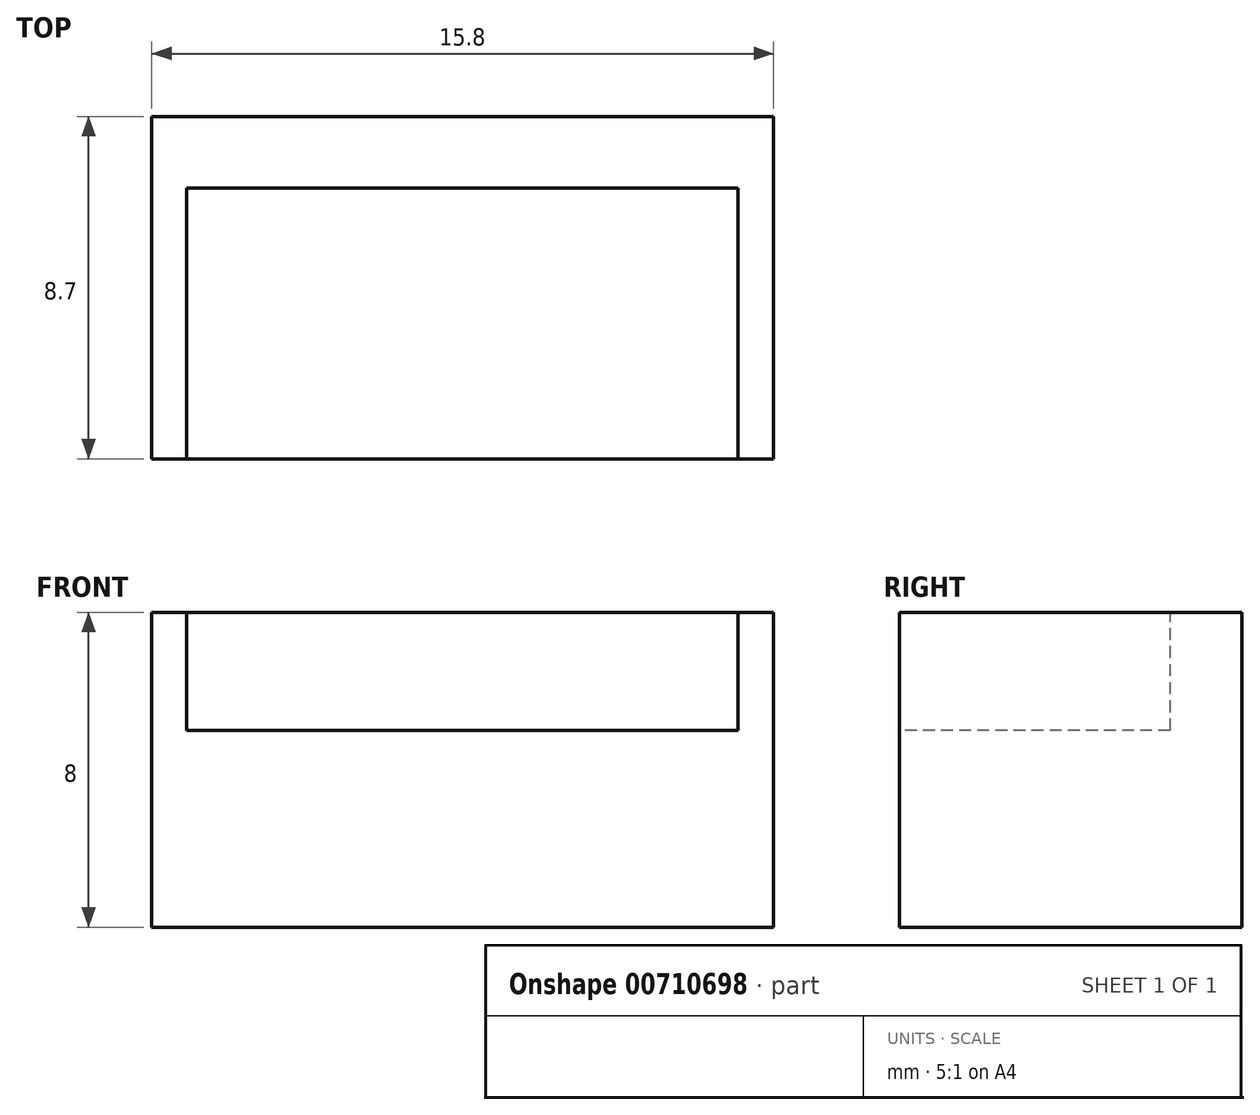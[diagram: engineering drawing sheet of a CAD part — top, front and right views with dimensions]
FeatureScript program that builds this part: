
annotation { "Feature Type Name" : "Feature", "Feature Type Description" : "" }
export const myFeature = defineFeature(function(context is Context, id is Id, definition is map)
    precondition{}
    {
        {
            var Q0;
            Q0=qCreatedBy(makeId("Top.planeOp"),FACE);
            var sketch = newSketch(context, id + "F0", { "sketchPlane" : qUnion([Q0])});
            skLineSegment(sketch, "E0.bottom", {"start": v(0, 0) * mm, "end": v(15.8, 0) * mm});
            skLineSegment(sketch, "E0.top", {"start": v(0, -8.7) * mm, "end": v(15.8, -8.7) * mm});
            skLineSegment(sketch, "E0.left", {"start": v(0, 0) * mm, "end": v(0, -8.7) * mm});
            skLineSegment(sketch, "E0.right", {"start": v(15.8, 0) * mm, "end": v(15.8, -8.7) * mm});
            skSolve(sketch);
        }
        {
            var Q0;
            Q0=makeQuery(id+"F0.imprint","IMPRINT",FACE,{"disambiguationData":[TD([[makeQuery(id+"F0.imprint","IMPRINT",EDGE,{"derivedFrom":sQuery(id+"F0.wireOp",EDGE,"E0.bottom")}),-1.0]])]});
            extrude(context, id + "F1", {"entities" : qUnion([Q0]), "depth" : 8 * mm, "offsetDistance" : 25 * mm});
        }
        {
            var Q0;
            Q0=makeQuery(id+"F1.opExtrude","CAP_FACE",FACE,{"disambiguationData":[OSD([sQuery(id+"F0.wireOp",EDGE,"E0.bottom"),sQuery(id+"F0.wireOp",EDGE,"E0.top"),sQuery(id+"F0.wireOp",EDGE,"E0.left"),sQuery(id+"F0.wireOp",EDGE,"E0.right")])],"isStart":false});
            var sketch = newSketch(context, id + "F2", { "sketchPlane" : qUnion([Q0])});
            skLineSegment(sketch, "E1.0", {"start": v(0, -8.7) * mm, "end": v(15.8, -8.7) * mm});
            skLineSegment(sketch, "E2.bottom", {"start": v(0.9, -1.82) * mm, "end": v(14.9, -1.82) * mm});
            skLineSegment(sketch, "E2.top", {"start": v(0.9, -8.7) * mm, "end": v(14.9, -8.7) * mm});
            skLineSegment(sketch, "E2.left", {"start": v(0.9, -1.82) * mm, "end": v(0.9, -8.7) * mm});
            skLineSegment(sketch, "E2.right", {"start": v(14.9, -1.82) * mm, "end": v(14.9, -8.7) * mm});
            skSolve(sketch);
        }
        {
            var Q0;
            Q0 = qSketchRegion(id + "F2", true);
            extrude(context, id + "F3", {"entities" : qUnion([Q0]), "operationType" : NewBodyOperationType.REMOVE, "oppositeDirection" : true, "depth" : 3 * mm, "offsetDistance" : 25 * mm});
        }
    });
